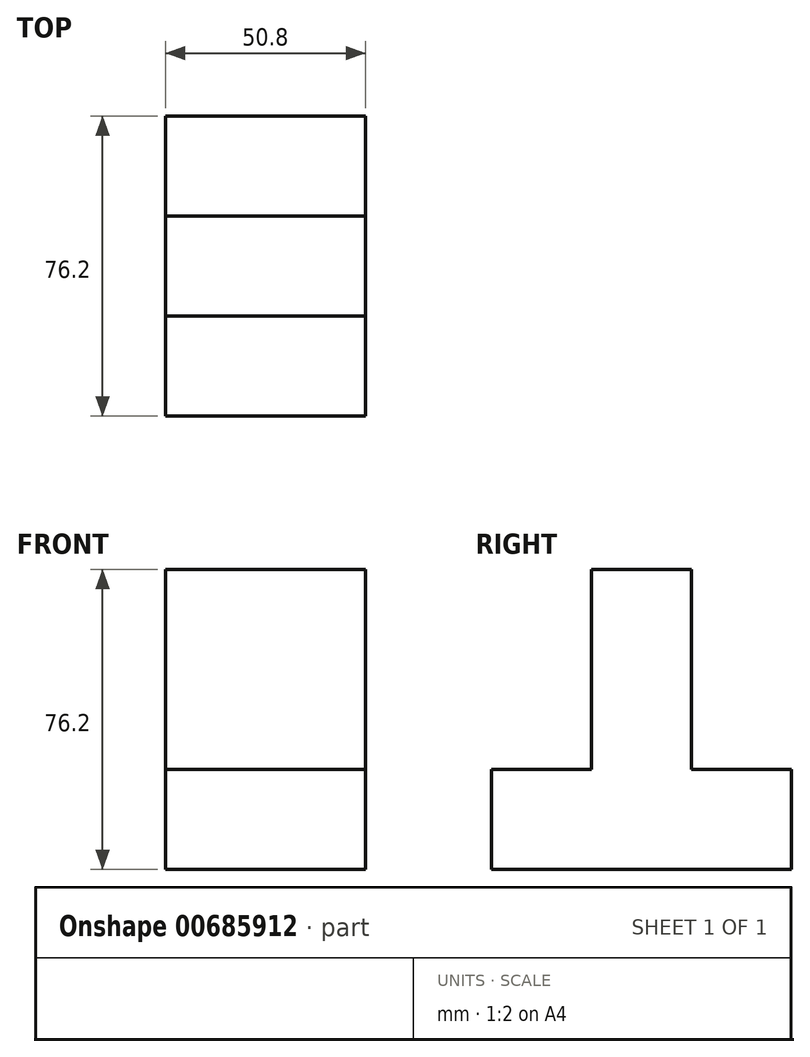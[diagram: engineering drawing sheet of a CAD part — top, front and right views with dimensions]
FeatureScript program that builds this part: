
annotation { "Feature Type Name" : "Feature", "Feature Type Description" : "" }
export const myFeature = defineFeature(function(context is Context, id is Id, definition is map)
    precondition{}
    {
        {
            var Q0;
            Q0=qCreatedBy(makeId("Right.planeOp"),FACE);
            var sketch = newSketch(context, id + "F0", { "sketchPlane" : qUnion([Q0])});
            skLineSegment(sketch, "E0", {"start": v(0, -40.38) * mm, "end": v(-50.8, -40.38) * mm});
            skLineSegment(sketch, "E1", {"start": v(-50.8, -40.38) * mm, "end": v(-50.8, -14.98) * mm});
            skLineSegment(sketch, "E2", {"start": v(-50.8, -14.98) * mm, "end": v(-25.4, -14.98) * mm});
            skLineSegment(sketch, "E3", {"start": v(-25.4, -14.98) * mm, "end": v(-25.4, 35.82) * mm});
            skLineSegment(sketch, "E4", {"start": v(-25.4, 35.82) * mm, "end": v(0, 35.82) * mm});
            skLineSegment(sketch, "E5", {"start": v(0, 35.82) * mm, "end": v(0, -14.98) * mm});
            skLineSegment(sketch, "E6", {"start": v(0, -14.98) * mm, "end": v(25.4, -14.98) * mm});
            skLineSegment(sketch, "E7", {"start": v(25.4, -14.98) * mm, "end": v(25.4, -40.38) * mm});
            skLineSegment(sketch, "E8", {"start": v(25.4, -40.38) * mm, "end": v(0, -40.38) * mm});
            skSolve(sketch);
        }
        {
            var Q0;
            Q0 = qSketchRegion(id + "F0", true);
            extrude(context, id + "F1", {"entities" : qUnion([Q0]), "depth" : 50.8 * mm, "offsetDistance" : 25.4 * mm});
        }
    });
